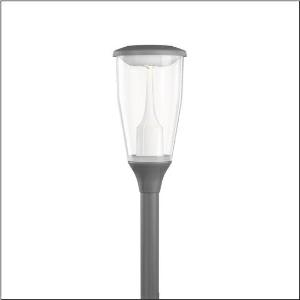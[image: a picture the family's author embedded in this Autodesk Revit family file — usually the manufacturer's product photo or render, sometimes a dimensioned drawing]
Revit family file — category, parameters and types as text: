
# Revit family: dl_11_iq___p1_0a_5xa5575bf14hp00022_48d3
name_source: partatom
category: Lighting Fixtures
units: mm (PartAtom-declared; Revit-internal decimal feet)

## family parameters
Cut with Voids When Loaded = No
Host = Face
Light Source = No
Part Type = Normal
Room Calculation Point = No
Round Connector Dimension = Use Diameter
Shared = No

## types (1)
- --- (1 x LED, 3950 lm, 33.6 W, 2200K)
    Apparent Load = 34 VA
    CIE Flux Codes = 23 60 93 95 100
    Color Rendering = 70
    Color Temperature = 2200K
    Default Elevation = 1800 mm
    Description = DL 11 iQ, mast luminaire, Module 540 iQ-SR, primary light control with 3 zone facetted reflector, of plastic, silver coated, highly specular, structured, primary optical cover: cover, of PMMA, transparent, light distribution: P1.0a, light emission: direct distribution, primary light characteristic: asymmetric, installation type: post-top, LED, High Power LED, light colour: 722, colour temperature: 2200K, control: Street-Remote, Auto-Match, Temp-Guard, Lumen-Switch, Night-Set, Smart-Wire, Light-Fading, Desk-Remote (wireless, voltage-free reading and setting of iQ features in the workshop via application-optimized NFC function/RFID function), optimised constant luminous flux control (CLO 2.0), mains connection: 220..240V, AC, 50/60Hz, connection cable pre-assembled, cable length: 5,5m, wiring characteristics: H07RN-F, 5-core, 1.5mm², start of lifetime: 34W, end of service life: 36W, luminaire housing, upper part, of diecast aluminium, coated, Siteco® metallic grey (DB 702S), spigot size: 76mm (post-top), post-top mast mounting element, of diecast aluminium, coated, Siteco® metallic grey (DB 702S), Module 540 iQ-SR, traffic white (RAL 9016), equipment: Power, protection rating (complete): IP66, insulation class (complete): insulation class II (safety insulation), certification: CE, ENEC, ENEC+, VDE, packaging unit: 1 piece

Light Distribution: P1.0a
    Height = 665 mm
    Lamp = 1 x LED
    Lamp Light Flux = 3950 lm
    Lamp Power = 33.6 W
    Lamp count = 1
    Length = 334 mm
    Luminous efficacy = 118 lm/W
    Manufacturer = Siteco
    ModVariant = No
    Model = 5XA5575BF14HP00022
    Number of Poles = 1
    OnlyDefault = Yes
    Power Factor = 1
    Product Name = DL 11 iQ | P1.0a
    Product group = mast luminaire | pylon top
    ProductGroupID = 6100
    Protection Class = Protection class II
    Protection Degree = IP 66
    RLX_Detail_Level = 1
    RLX_Emergency_Light_Flux = 0 lm
    RLX_Emergency_Type = 0
    RLX_Emergency_Type_DB = No
    RlxData = <blob elided: 103069 chars, md5=86712574>
    Socket = socket
    Standby Power = 0 W
    System Light Flux = 3950 lm
    System Power = 34 W
    Type Comments = factory setting: luminous flux: 100 % | dim-lin: 254 | 695 mA
    Type Image = l_1258354.jpg
    URL = http://relux.com
    VarID = @adj_021859
    Voltage = 0 V
    Weight = 0.00 kg
    Width = 0 mm  [stored 0 ft]

note: [stored X ft] marks values corroborated as IEEE doubles in the binary element streams (Revit-internal decimal feet)

## geometry (parser evidence)
native form markers: Blend x4, Sweep x8
no freeform markers — native parametric forms only
